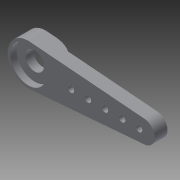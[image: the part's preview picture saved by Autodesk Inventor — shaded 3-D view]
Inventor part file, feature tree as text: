
AUTODESK INVENTOR PART (.ipt)
format: ipt  version: 2015 SP2 (Build 190223200, 223)  size: 143,872 bytes
history: native  units: mm
features: sketch x7, extrude x4, hole x3, fillet x1
ambient origin geometry x8: Origin, YZ Plane, XZ Plane, XY Plane, X Axis, Y Axis, Z Axis, Center Point
bodies: Solid1 (feature_tree)
feature tree (15):
  extrude  "Extrusion1"  Depth=11.314mm
  extrude  "Extrusion2"  Depth=36.0mm
  fillet  "Fillet1"  Radius=36.0mm
  sketch  "Sketch4"  dims[d5=7.0mm d6=4.0mm d7=0.0mm]
  extrude  "Extrusion3"  Depth=4.0mm TaperAngle=0.0deg
  extrude  "Extrusion4"  Depth=10.0mm
  hole  "Hole1"  [1 undecoded]
  hole  "Hole2"  [1 undecoded]
  hole  "Hole4"  [1 undecoded]
  sketch  "Sketch1"  dims[d0=12.9mm d1=11.314mm]
  sketch  "Sketch2"  dims[d2=5.7mm d3=3.0mm d4=36.0mm]
  sketch  "Sketch5"  dims[d8=1.5mm d9=0.0mm d10=10.0mm]
  sketch  "Sketch6"  dims[d11=5.8mm d12=3.0mm]
  sketch  "Sketch7"  dims[d13=0.5mm d14=0.0mm d15=2.0mm d16=0.0mm]
  sketch  "Sketch9"  dims[d17=5.8mm d18=0.5mm d19=0.0mm d20=3.0mm d21=6.0mm d22=4.0mm d23=2.0mm d24=90.0deg d25=8.0mm d26=20.594885mm d27=5.8mm d28=5.8mm d29=6.0mm d30=4.0mm d31=2.0mm d32=90.0deg d33=2.0mm d34=20.594885mm d47=2.0mm d48=6.0mm d49=4.0mm d50=2.0mm d51=90.0deg d52=1.0mm d53=20.594885mm d54=1.0mm d55=1.0mm]
note: 3 required parameter values undecoded (feature->parameter linkage not recoverable at this tier; creation-order binding heuristic only, values carry confidence <= 0.55)
